# Revit family: pefy-p224_280smg9_50Hz
name_source: partatom
category: 機械設備
units: mm (PartAtom-declared; Revit-internal decimal feet)

## family parameters
OmniClass タイトル = Split System Air Conditioning Units
OmniClass 番号 = 23.75.10.24.21.27.27
パーツ タイプ = 標準
ロード時にボイドで切り取り = いいえ
丸型コネクタ寸法 = 直径を使用
作業面ベース = いいえ
共有 = いいえ
常に垂直 = はい
部屋計算ポイント = はい

## types (2) — shared parameters
Clearance Back = 50  [stored 0.164042 ft]
Clearance Bottom = 20  [stored 0.0656168 ft]
Clearance Front = 680  [stored 2.23097 ft]
Clearance Left = 1300  [stored 4.26509 ft]
Clearance Right = 50  [stored 0.164042 ft]
Clearance Top = 20  [stored 0.0656168 ft]
Depth = 1120  [stored 3.67454 ft]
Height = 470  [stored 1.54199 ft]
IfcExportAs = IfcUnitaryEquipmentType
IfcExportType = AIRCONDITIONINGUNIT
OmniClassCode = 23-751024212727
RAサイズ_D = 420  [stored 1.37795 ft]
RAサイズ_W = 1100
SAサイズ_D = 340  [stored 1.11549 ft]
SAサイズ_W = 1100
S_H = 490  [stored 1.60761 ft]
URL = https://www.mitsubishielectric.co.jp
Uniclass2015Code = Pr_70_65_03_84
Uniclass2015Title = Split coil remote air cooled condensing units
Uniclass2015Version = Systems v1.9
ケーブルサイズ = 0 mm
サービススペース = はい
ドレン管_横 = 489  [stored 1.60433 ft]
ドレン管_縦 = 327
ドレン管径 = 32 mm
仕様書バージョン = Version1.0
企業コード = 108420
冷媒ガス管_横 = 249  [stored 0.816929 ft]
冷媒ガス管_縦 = 164  [stored 0.538058 ft]
冷媒液管_横 = 95
冷媒液管_縦 = 44  [stored 0.144357 ft]
冷媒液管径 = 10 mm
冷媒管径 = 100 mm
冷媒高低圧ガス管径 = 0 mm
分類コード = 50053003221070
加湿給水管径 = 0 mm
参照している仕様書等のバージョン = 公共建築工事標準仕様書（機械設備工事編）平成31年度版
吊り位置X = 1326  [stored 4.35039 ft]
吊り位置Y = 1034  [stored 3.39239 ft]
吊り幅 = 61  [stored 0.200131 ft]
周波数 = 50 Hz
呼称 = 室内機_天井吊(隠ぺい)形(両ダクト形)
形式 = 天井吊（隠ぺい）形（両ダクト形）
推奨ブレーカー容量 = 0 A
本体マテリアル = <カテゴリ別>
極数 = 3
機外静圧 = 150.0 Pa
法定耐用年数 = 15
消費電力_加湿器 = 0.00 kW
消費電力_電気ヒーター = 0.00 kW
点検口 = はい
点検口位置 = 200  [stored 0.656168 ft]
点検口設置範囲 = 800  [stored 2.62467 ft]
発停方法 = 付属スイッチ
相 = 1
相_電気ヒーター = 1
積算_科目 = 1 空気調和設備
符号 = ACP_CID
製品リリース年月 = 2022年9月15日
製品出荷対象 = 国内
製造元 = 三菱電機株式会社
設置方法 = 天井吊(隠ぺい)形
設計冷房能力 = 0 kW
設計冷房能力_顕熱 = 0 kW
設計暖房能力 = 0.00 kW
説明 = ビル用マルチエアコン 天井埋込形　室内機
負荷分類 = 3_ファン類
運転質量 = 0.00 kg
電動機出力_送風機 = 0.87 kW
電圧 = 200 V
電圧_電気ヒーター = 0 V
zero-valued in all types: Width, 有効加湿量, 電源_H

## per-type parameters (varying)
| type | MAX風量 | MIN風量 | 冷媒ガス管径 | 冷媒管径符号 | 冷房能力 | 暖房能力 | 消費電力 | 消費電力_冷房 | 消費電力_暖房 | 製品質量 | 質量 | 音響パワーレベル(dB) | 音響パワーレベル（弱）(dB) | 風量 | 風量（m3／min） | 風量（弱）（m3／min） |
| PEFY-P224SMG9 | 4320.0 m³/h | 3000.0 m³/h | 19 mm | Be | 22.4 kW | 25.00 kW | 0.68 kW | 0.68 kW | 0.68 kW | 97.00 kg | 116.40 kg | 67 | 65 | 4320.0 m³/h | 72 | 50 |
| PEFY-P280SMG9 | 5040.0 m³/h | 3480.0 m³/h | 22 mm | Bf | 28 kW | 31.50 kW | 0.92 kW | 0.92 kW | 0.92 kW | 100.00 kg | 120.00 kg | 71 | 70 | 5040.0 m³/h | 84 | 58 |

note: column(s) folded — value = type name in every type: モデル

note: [stored X ft] marks values corroborated as IEEE doubles in the binary element streams (Revit-internal decimal feet)

## geometry (parser evidence)
native form markers: Blend x2
no freeform markers — native parametric forms only
